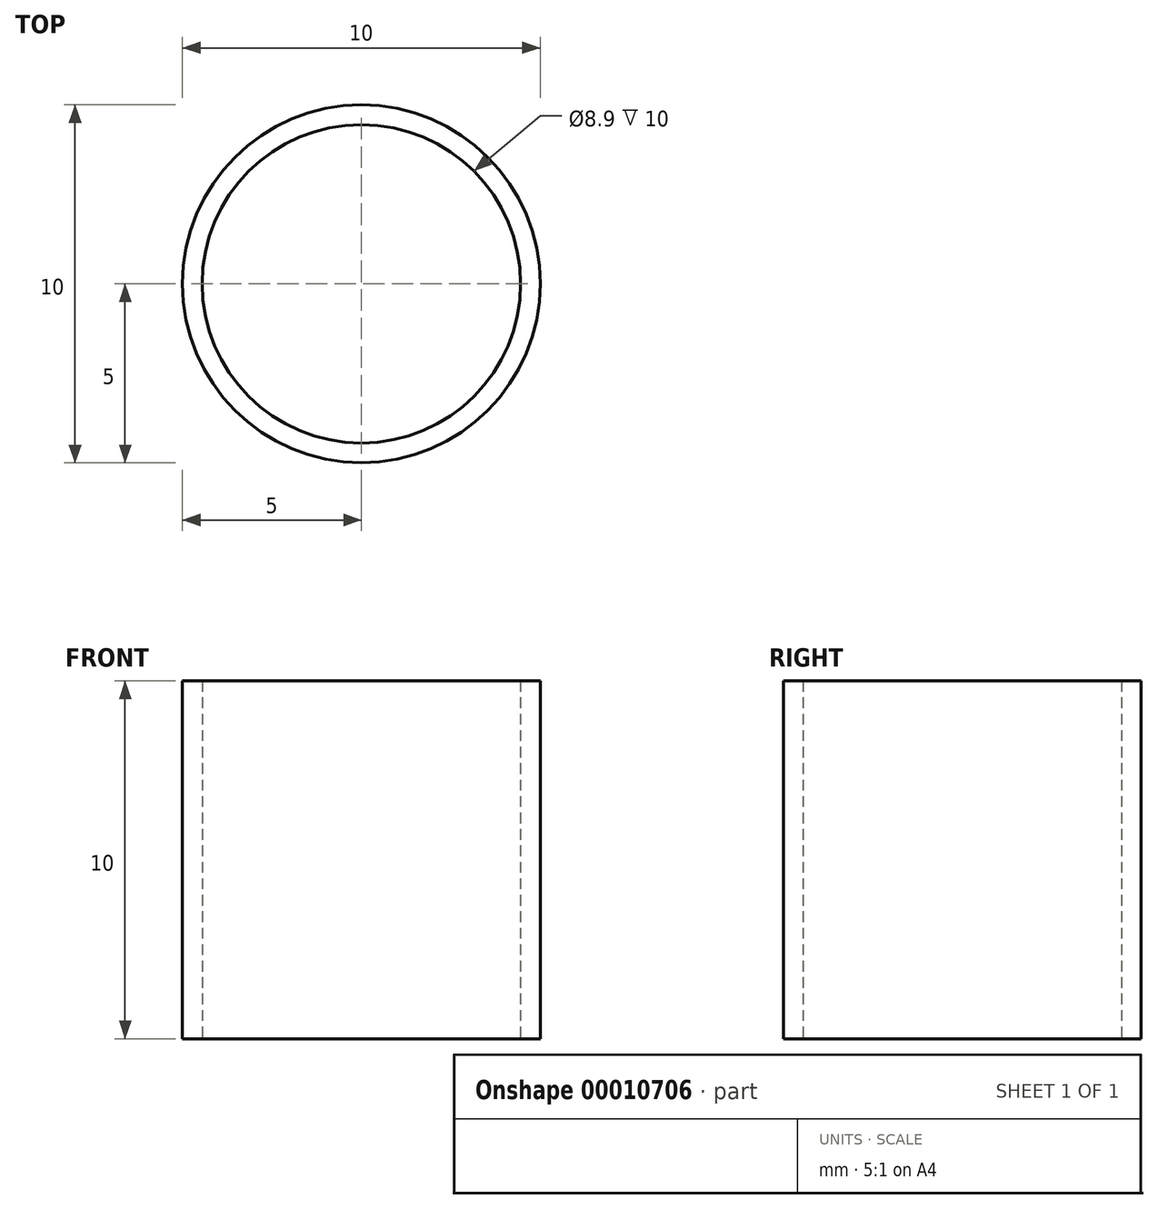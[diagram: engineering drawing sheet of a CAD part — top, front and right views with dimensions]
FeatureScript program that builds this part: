
annotation { "Feature Type Name" : "Feature", "Feature Type Description" : "" }
export const myFeature = defineFeature(function(context is Context, id is Id, definition is map)
    precondition{}
    {
        {
            var Q0;
            Q0=qCreatedBy(makeId("Top.planeOp"),FACE);
            var sketch = newSketch(context, id + "F0", { "sketchPlane" : qUnion([Q0])});
            skCircle(sketch, "E0", {"center": v(0, 0) * mm, "radius": 4.45 * mm});
            skCircle(sketch, "E1", {"center": v(0, 0) * mm, "radius": 5 * mm});
            skSolve(sketch);
        }
        {
            var Q0;
            Q0=makeQuery(id+"F0.imprint","IMPRINT",FACE,{"disambiguationData":[TD([[makeQuery(id+"F0.imprint","IMPRINT",EDGE,{"derivedFrom":sQuery(id+"F0.wireOp",EDGE,"E0")}),-1.0]])]});
            extrude(context, id + "F1", {"entities" : qUnion([Q0]), "depth" : 10 * mm});
        }
    });
